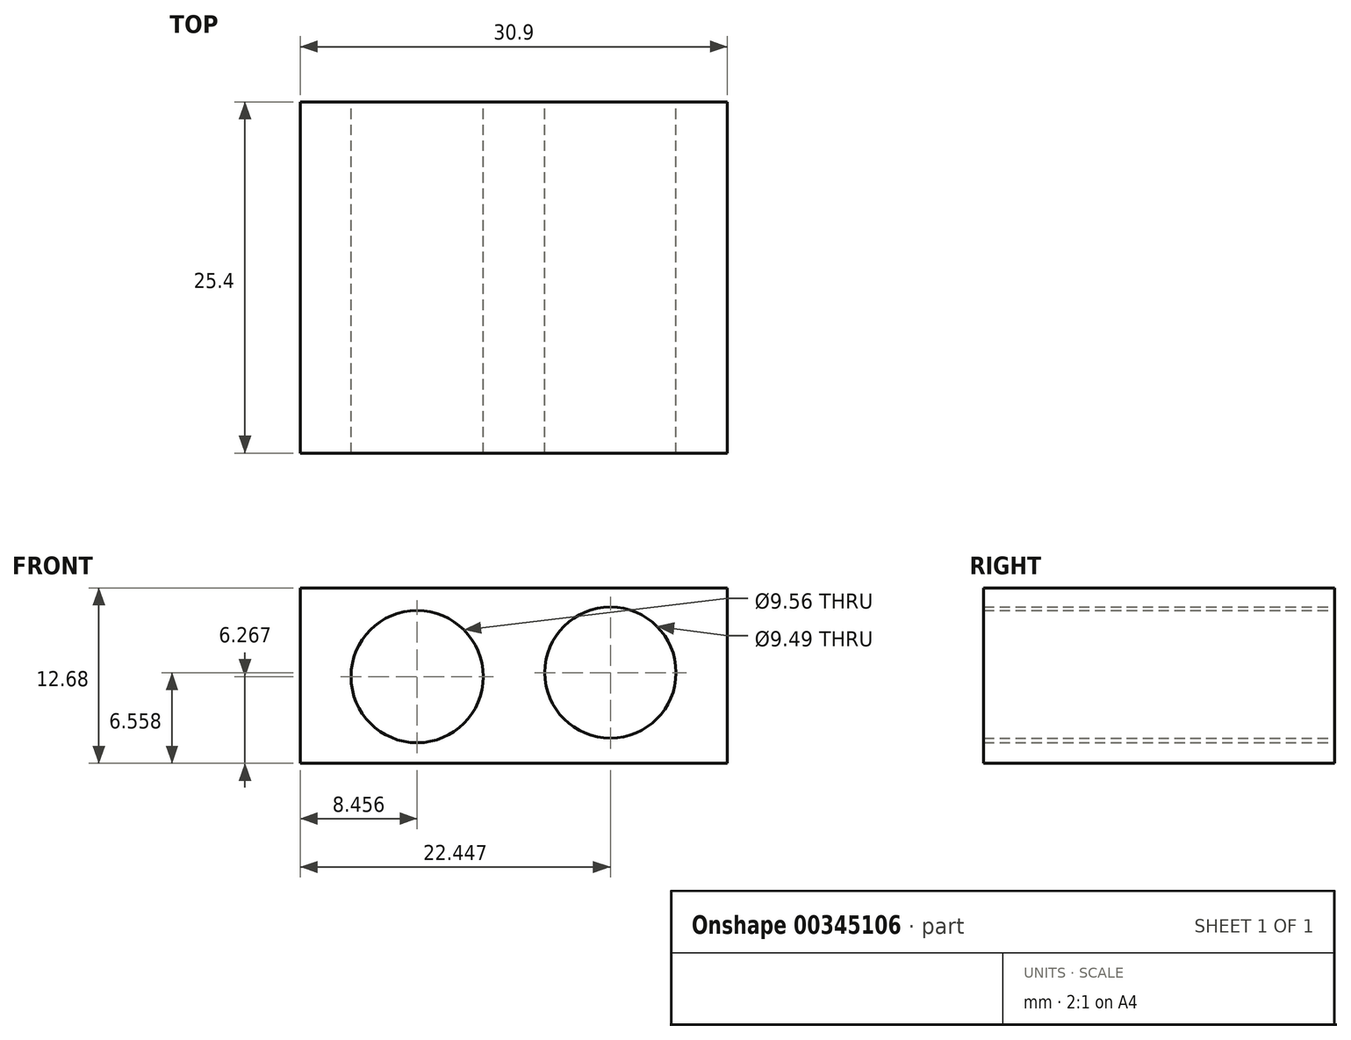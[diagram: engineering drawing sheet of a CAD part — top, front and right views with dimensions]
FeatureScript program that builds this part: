
annotation { "Feature Type Name" : "Feature", "Feature Type Description" : "" }
export const myFeature = defineFeature(function(context is Context, id is Id, definition is map)
    precondition{}
    {
        {
            var Q0;
            Q0=qCreatedBy(makeId("Front.planeOp"),FACE);
            var sketch = newSketch(context, id + "F0", { "sketchPlane" : qUnion([Q0])});
            skLineSegment(sketch, "E0.bottom", {"start": v(0, 0) * mm, "end": v(-30.9, 0) * mm});
            skLineSegment(sketch, "E0.top", {"start": v(0, 12.68) * mm, "end": v(-30.9, 12.68) * mm});
            skLineSegment(sketch, "E0.left", {"start": v(0, 0) * mm, "end": v(0, 12.68) * mm});
            skLineSegment(sketch, "E0.right", {"start": v(-30.9, 0) * mm, "end": v(-30.9, 12.68) * mm});
            skCircle(sketch, "E1", {"center": v(-22.44, 6.27) * mm, "radius": 4.78 * mm});
            skCircle(sketch, "E2", {"center": v(-8.45, 6.56) * mm, "radius": 4.74 * mm});
            skSolve(sketch);
        }
        {
            var Q0;
            Q0 = qSketchRegion(id + "F0", true);
            extrude(context, id + "F1", {"entities" : qUnion([Q0]), "depth" : 25.4 * mm});
        }
    });
